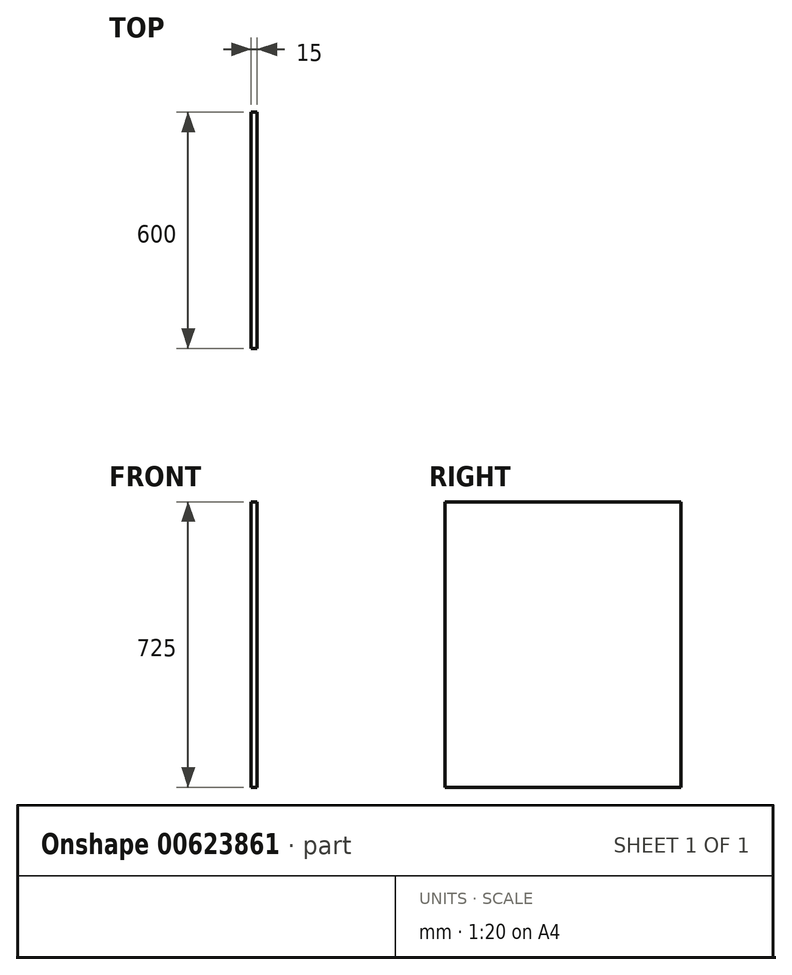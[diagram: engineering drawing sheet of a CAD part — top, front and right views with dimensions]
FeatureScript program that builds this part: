
annotation { "Feature Type Name" : "Feature", "Feature Type Description" : "" }
export const myFeature = defineFeature(function(context is Context, id is Id, definition is map)
    precondition{}
    {
        {
            var Q0;
            Q0=qCreatedBy(makeId("Top.planeOp"),FACE);
            var sketch = newSketch(context, id + "F0", { "sketchPlane" : qUnion([Q0])});
            skLineSegment(sketch, "E0.bottom", {"start": v(0, 600) * mm, "end": v(15, 600) * mm});
            skLineSegment(sketch, "E0.top", {"start": v(0, 0) * mm, "end": v(15, 0) * mm});
            skLineSegment(sketch, "E0.left", {"start": v(0, 600) * mm, "end": v(0, 0) * mm});
            skLineSegment(sketch, "E0.right", {"start": v(15, 600) * mm, "end": v(15, 0) * mm});
            skSolve(sketch);
        }
        {
            var Q0;
            Q0 = qSketchRegion(id + "F0", true);
            extrude(context, id + "F1", {"entities" : qUnion([Q0]), "depth" : 725 * mm, "offsetDistance" : 25 * mm});
        }
    });
